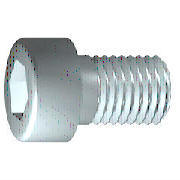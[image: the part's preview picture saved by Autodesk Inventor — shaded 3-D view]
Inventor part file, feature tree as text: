
AUTODESK INVENTOR PART (.ipt)
format: ipt  version: 2017 (Build 210142000, 142)  size: 195,584 bytes
history: native  units: mm (DEFAULTED — no unit token found)
features: sketch x2, other x1, extrude x1, plane x1, fillet x1
ambient origin geometry x7: Origin, YZ Plane, XY Plane, X Axis, Y Axis, Z Axis, Center Point
bodies: Solid1 (feature_tree)
feature tree (6):
  other  "Corps"
  extrude  "Rainure"  Depth=6.75mm
  plane  "Work Plane1"
  fillet  "Fillet2"  Radius=0.306825mm
  sketch  "Esquisse1"
  sketch  "Esquisse2"
